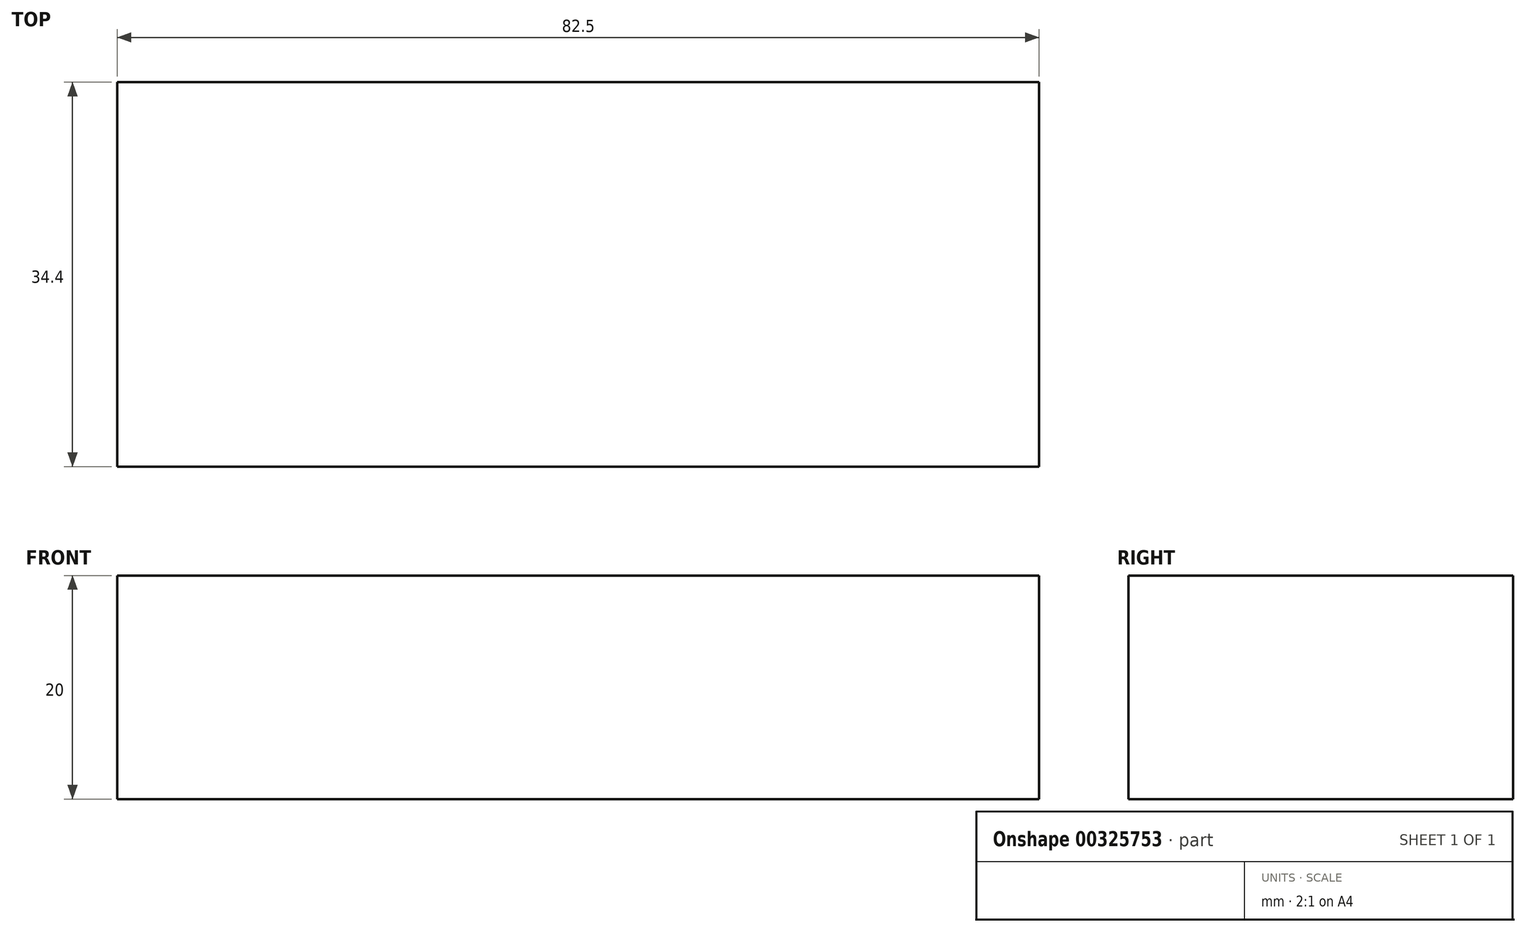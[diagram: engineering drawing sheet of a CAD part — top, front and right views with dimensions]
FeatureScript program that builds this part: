
annotation { "Feature Type Name" : "Feature", "Feature Type Description" : "" }
export const myFeature = defineFeature(function(context is Context, id is Id, definition is map)
    precondition{}
    {
        {
            var Q0;
            Q0=qCreatedBy(makeId("Front.planeOp"),FACE);
            var sketch = newSketch(context, id + "F0", { "sketchPlane" : qUnion([Q0])});
            skLineSegment(sketch, "E0.bottom", {"start": v(41.25, -10) * mm, "end": v(-41.25, -10) * mm});
            skLineSegment(sketch, "E0.top", {"start": v(41.25, 10) * mm, "end": v(-41.25, 10) * mm});
            skLineSegment(sketch, "E0.left", {"start": v(41.25, -10) * mm, "end": v(41.25, 10) * mm});
            skLineSegment(sketch, "E0.right", {"start": v(-41.25, -10) * mm, "end": v(-41.25, 10) * mm});
            skPoint(sketch, "E0.middle", {"position": v(0, 0) * mm});
            skSolve(sketch);
        }
        {
            var Q0;
            Q0=makeQuery(id+"F0.imprint","IMPRINT",FACE,{"disambiguationData":[TD([[makeQuery(id+"F0.imprint","IMPRINT",EDGE,{"derivedFrom":sQuery(id+"F0.wireOp",EDGE,"E0.bottom")}),-1.0]])]});
            extrude(context, id + "F1", {"entities" : qUnion([Q0]), "depth" : 34.4 * mm});
        }
    });
